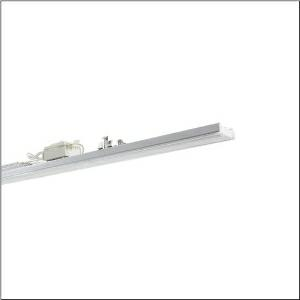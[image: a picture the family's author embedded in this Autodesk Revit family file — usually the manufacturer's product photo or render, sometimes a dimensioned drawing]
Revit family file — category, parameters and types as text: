
# Revit family: licross_r__21_recessed_mo_52te12dv4fxg3s_e0fc
name_source: partatom
category: Lighting Fixtures
units: mm (PartAtom-declared; Revit-internal decimal feet)

## family parameters
Cut with Voids When Loaded = No
Host = Face
Light Source = No
Part Type = Normal
Room Calculation Point = No
Round Connector Dimension = Use Diameter
Shared = No

## types (1)
- --- (1 x LED, 950 lm, 5.5 W, 4000K)
    Apparent Load = 6 VA
    CIE Flux Codes = 72 92 99 100 100
    Color Rendering = 80
    Color Temperature = 4000K
    Default Elevation = 1800 mm
    Description = Licross® 21 Recessed MO, luminaire insert, of sheet steel, galvanised, coil coated, white, length: 2.250mm, width: 66mm, height: 67mm, LED rated luminous flux: 15.420lm, light colour: 840, control gear: DALI 2 (for two DALI lines), with plug, 6-pole, with phase selection, for trunking rail, 14-core, mains connection: 220..240V, AC, 50/60Hz, rated input power: 89W, for trunking rail, 14-core, halogen-free wiring, for emergency light function, converter,control gear: single battery element, battery: LiFePO4, 9Ah, primary optical cover: cover, of PMMA, light emission: direct distribution, primary light characteristic: symmetric, protection rating (complete): IP54, insulation class (complete): insulation class I (protective earthing), certification: CE, UKCA, protection symbol: D if used in an environment with non-conductive dust loads with corresponding accessories, impact resistance: IK06, permissible ambient temperature for indoor applications: +5..+35°C, standard: EN 60598-2-22, LABS conformity tested according to VDMA 24364:2018-05, reducing of maximum allowable ambient temperature of 5°C with ceiling mounting, corresponds to IFS (International Featured Standards) requirements for safety and quality in the food industry, packaging unit: 1 piece
    Height = 58 mm
    Lamp = 1 x LED
    Lamp Light Flux = 950 lm
    Lamp Power = 5.5 W
    Lamp count = 1
    Length = 2250 mm
    Luminous efficacy = 173 lm/W
    Manufacturer = Siteco
    ModVariant = No
    Model = 52TE12DV4FXG3S
    Mounting Place = Ceiling
    Mounting Type = Pendant
    Number of Poles = 1
    OnlyDefault = Yes
    Power Factor = 1
    Product Name = Licross® 21 Recessed MO
    Product group = luminaire insert
    ProductGroupID = 902
    Protection Class = Protection class I
    Protection Degree = IP 54
    RLX_Detail_Level = 1
    RLX_Emergency_Light_Flux = 0 lm
    RLX_Emergency_Type = 0
    RLX_Emergency_Type_DB = No
    RlxData = <blob elided: 29949 chars, md5=07b4ddba>
    Socket = socket
    Standby Power = 0 W
    System Light Flux = 950 lm
    System Power = 6 W
    Type Comments = : emergency light operation: 3 h
    Type Image = l_1296930.jpg
    URL = http://relux.com
    VarID = @adj_110070
    Voltage = 0 V
    Weight = 0.00 kg
    Width = 66 mm

## geometry (parser evidence)
native form markers: Blend x4, Sweep x8
no freeform markers — native parametric forms only
